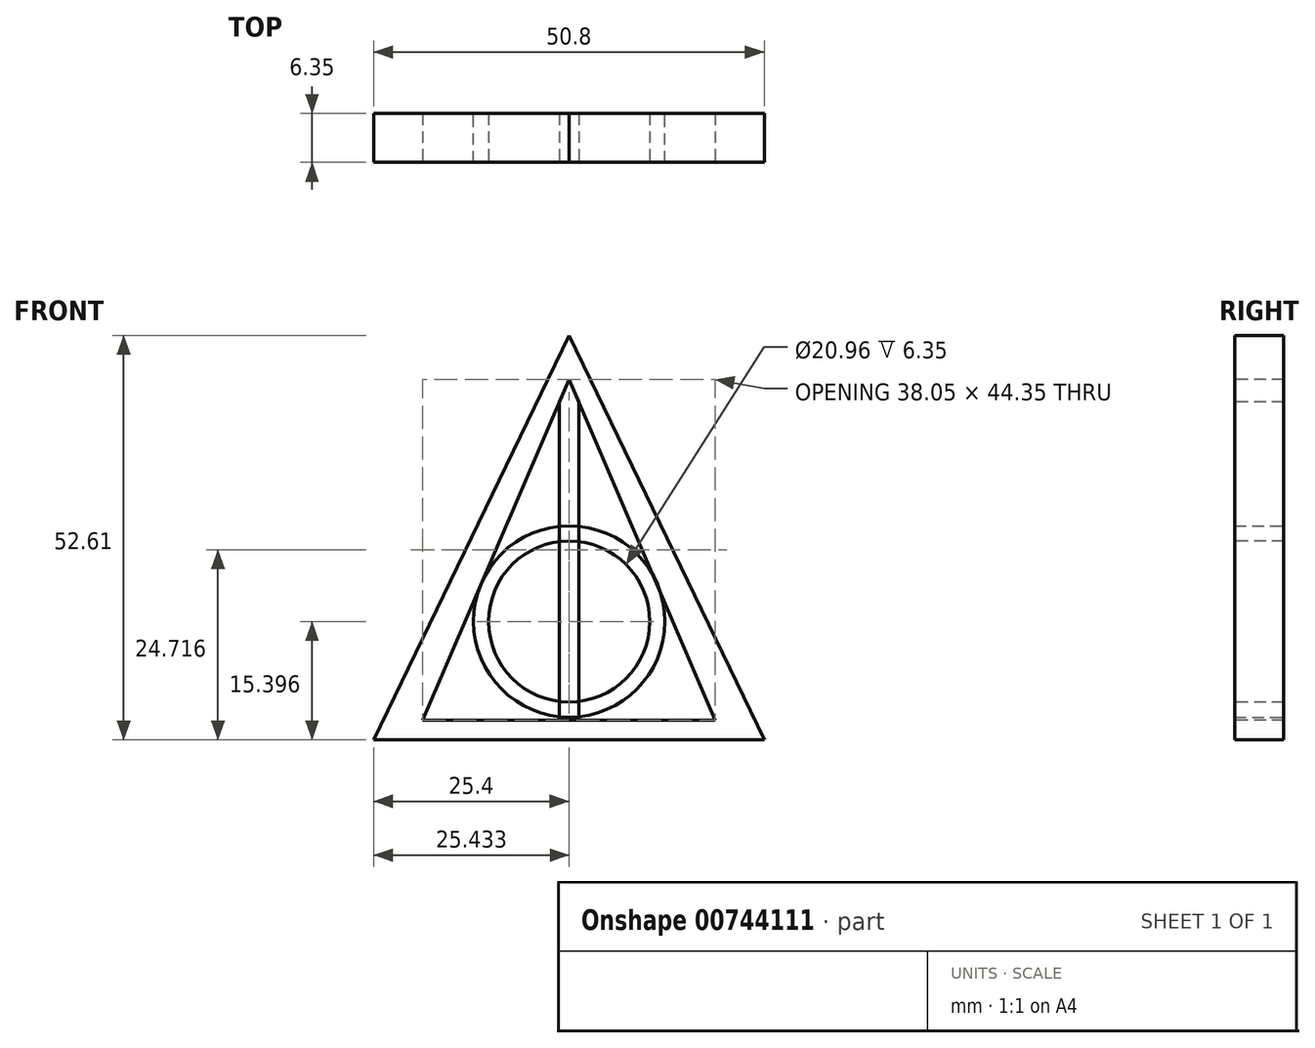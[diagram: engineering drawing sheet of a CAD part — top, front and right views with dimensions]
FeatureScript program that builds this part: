
annotation { "Feature Type Name" : "Feature", "Feature Type Description" : "" }
export const myFeature = defineFeature(function(context is Context, id is Id, definition is map)
    precondition{}
    {
        {
            var Q0;
            Q0=qCreatedBy(makeId("Front.planeOp"),FACE);
            var sketch = newSketch(context, id + "F0", { "sketchPlane" : qUnion([Q0])});
            skLineSegment(sketch, "E0", {"start": v(0, 0) * mm, "end": v(50.8, 0) * mm});
            skLineSegment(sketch, "E1", {"start": v(50.8, 0) * mm, "end": v(25.4, 52.6) * mm});
            skLineSegment(sketch, "E2", {"start": v(25.4, 52.6) * mm, "end": v(0, 0) * mm});
            skSolve(sketch);
        }
        {
            var Q0;
            Q0 = qSketchRegion(id + "F0", true);
            extrude(context, id + "F1", {"entities" : qUnion([Q0]), "depth" : 6.35 * mm, "offsetDistance" : 25.4 * mm});
        }
        {
            var Q0;
            Q0=makeQuery(id+"F1.opExtrude","CAP_FACE",FACE,{"disambiguationData":[OSD([sQuery(id+"F0.wireOp",EDGE,"E0"),sQuery(id+"F0.wireOp",EDGE,"E1"),sQuery(id+"F0.wireOp",EDGE,"E2")])],"isStart":false});
            var sketch = newSketch(context, id + "F2", { "sketchPlane" : qUnion([Q0])});
            skLineSegment(sketch, "E3", {"start": v(6.38, 2.54) * mm, "end": v(44.42, 2.54) * mm});
            skLineSegment(sketch, "E4", {"start": v(44.42, 2.54) * mm, "end": v(25.4, 46.9) * mm});
            skLineSegment(sketch, "E5", {"start": v(25.4, 46.9) * mm, "end": v(6.38, 2.54) * mm});
            skSolve(sketch);
        }
        {
            var Q0;
            Q0 = qSketchRegion(id + "F2", true);
            extrude(context, id + "F3", {"entities" : qUnion([Q0]), "operationType" : NewBodyOperationType.REMOVE, "oppositeDirection" : true, "depth" : 25.4 * mm, "offsetDistance" : 25.4 * mm});
        }
        {
            var Q0;
            Q0=makeQuery(id+"F1.opExtrude","CAP_FACE",FACE,{"disambiguationData":[OSD([sQuery(id+"F0.wireOp",EDGE,"E0"),sQuery(id+"F0.wireOp",EDGE,"E1"),sQuery(id+"F0.wireOp",EDGE,"E2")])],"isStart":false});
            var sketch = newSketch(context, id + "F4", { "sketchPlane" : qUnion([Q0])});
            skLineSegment(sketch, "E6", {"start": v(24.13, 43.93) * mm, "end": v(24.13, 2.54) * mm});
            skLineSegment(sketch, "E7", {"start": v(24.13, 2.54) * mm, "end": v(26.67, 2.54) * mm});
            skLineSegment(sketch, "E8", {"start": v(26.67, 2.54) * mm, "end": v(26.67, 43.93) * mm});
            skLineSegment(sketch, "E9", {"start": v(26.67, 43.93) * mm, "end": v(25.4, 46.9) * mm});
            skLineSegment(sketch, "E10", {"start": v(25.4, 46.9) * mm, "end": v(24.13, 43.93) * mm});
            skSolve(sketch);
        }
        {
            var Q0;
            Q0 = qSketchRegion(id + "F4", true);
            extrude(context, id + "F5", {"entities" : qUnion([Q0]), "oppositeDirection" : true, "depth" : 6.35 * mm, "offsetDistance" : 25.4 * mm});
        }
        {
            var Q0;
            Q0=qCreatedBy(makeId("Front.planeOp"),FACE);
            var sketch = newSketch(context, id + "F6", { "sketchPlane" : qUnion([Q0])});
            skCircle(sketch, "E11", {"center": v(25.43, 15.4) * mm, "radius": 12.45 * mm});
            skPoint(sketch, "E12", {"position": v(20.5, 26.82) * mm});
            skSolve(sketch);
        }
        {
            var Q0;
            Q0 = qSketchRegion(id + "F6", true);
            extrude(context, id + "F7", {"entities" : qUnion([Q0]), "depth" : 6.35 * mm, "offsetDistance" : 25.4 * mm});
        }
        {
            var Q0;
            Q0=makeQuery(id+"F7.opExtrude","CAP_FACE",FACE,{"disambiguationData":[OSD([sQuery(id+"F6.wireOp",EDGE,"E11")])],"isStart":false});
            var sketch = newSketch(context, id + "F8", { "sketchPlane" : qUnion([Q0])});
            skPoint(sketch, "E13", {"position": v(25.43, 15.4) * mm});
            skSolve(sketch);
        }
        {
            var Q0;
            Q0=sQuery(id+"F8.wireOp",VERTEX,"E13");
            var Q1;
            Q1=makeQuery(id+"F7.opExtrude","SWEPT_BODY",BODY,{"disambiguationData":[OSD([sQuery(id+"F6.wireOp",EDGE,"E11")])]});
            hole(context, id + "F9", {"style" : HoleStyle.SIMPLE, "endStyle" : HoleEndStyle.THROUGH, "holeDiameter" : 20.95 * mm, "majorDiameter" : 6.35 * mm, "isTappedThrough" : true, "tappedDepth" : 12.7 * mm, "tapClearance" : 3, "locations" : qUnion([Q0]), "scope" : qUnion([Q1])});
        }
        {
            var Q0;
            {var subQ0=sQuery(id+"F0.wireOp",EDGE,"E2");Q0=makeQuery(id+"FiPrxx1a5bdp3Fz_3.boolean.opBoolean","MERGE",FACE,{"derivedFrom":[makeQuery(id+"F1.opExtrude","SWEPT_FACE",FACE,{"disambiguationData":[OSD([subQ0])]}),makeQuery(id+"FiPrxx1a5bdp3Fz_3.opExtrude","SWEPT_FACE",FACE,{"disambiguationData":[OSD([subQ0])]})]});}
            var sketch = newSketch(context, id + "F10", { "sketchPlane" : qUnion([Q0])});
            skCircle(sketch, "E14", {"center": v(3.18, 58.42) * mm, "radius": 5.96 * mm});
            skSolve(sketch);
        }
        {
            var Q0;
            Q0 = qSketchRegion(id + "F10", true);
            extrude(context, id + "F11", {"entities" : qUnion([Q0]), "operationType" : NewBodyOperationType.ADD, "depth" : 6.35 * mm, "offsetDistance" : 25.4 * mm});
        }
        {
            var Q0;
            Q0=makeQuery(id+"F11.opExtrude","CAP_FACE",FACE,{"disambiguationData":[OSD([sQuery(id+"F10.wireOp",EDGE,"E14")])],"isStart":false});
            extrude(context, id + "F12", {"entities" : qUnion([Q0]), "operationType" : NewBodyOperationType.REMOVE, "oppositeDirection" : true, "depth" : 6.35 * mm, "offsetDistance" : 25.4 * mm});
        }
    });
